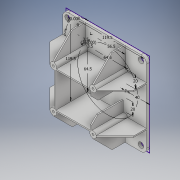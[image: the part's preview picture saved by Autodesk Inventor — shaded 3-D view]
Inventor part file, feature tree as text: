
AUTODESK INVENTOR PART (.ipt)
format: ipt  version: 2019.3 (Build 233278000, 278)  size: 249,344 bytes
history: native  units: mm
features: extrude x2, chamfer x2, other x1, fillet x1
ambient origin geometry x8: Origin, YZ Plane, XZ Plane, XY Plane, X Axis, Y Axis, Z Axis, Center Point
bodies: Body1 (feature_tree)
feature tree (6):
  other  "BasePlate"
  extrude  "Extrusion8"  Depth=56.5mm
  extrude  "Extrusion9"  Depth=40.0mm
  chamfer  "Chamfer3"  Distance=3.5mm
  chamfer  "Chamfer4"  Distance=3.5mm
  fillet  "Fillet3"  Radius=4.0mm
